# Revit family: CADS_AIRFLOWdev_AirflexPro_Round_DistributionBox_6PortNarrow_side_entry.rfa - HS
name_source: partatom
category: Duct Accessories
units: mm (PartAtom-declared; Revit-internal decimal feet)

## family parameters
Always vertical = Yes
Cut with Voids When Loaded = No
OmniClass Number = 23.75.00.00
OmniClass Title = Climate Control (HVAC)
Part Type = Breaks Into
Round Connector Dimension = Use Diameter
Shared = No
Work Plane-Based = No

## types (2) — shared parameters
6MonthlyMaintenance = Visually inspect system, clean the fan and ducting if necessary
AirflowRateRange = 54.0 L/s
AssemblyPlace = UNKNOWN
AssetType = FIXED
Body = CADS_AIRFLOWdev_SteelGalvanized
CEApproval = Yes
Color = Silver
Conn_IDia = 125 mm  [stored 0.410105 ft]
DurationUnit = Year
ExpectedServiceLife = 10
Finish = Lacquer
FireControlPanelLinks = No
Fitting Type = Ignore
Grade = Stainless
GrossWeight = 5.05 kg
Halfb1 = 150 mm  [stored 0.492126 ft]
ISO140001 = Yes
ISO90001 = Yes
IsExtendedWarranty = No
LongitudinalSeam = None
Manufacturer = Airflow Developments Ltd
ManufacturerAddress = Aidelle House
Lancaster Road
Cressex Business Park
High Wycombe
Bucks
HP123QP
ManufacturerTelephone = 01494 525252
ManufacturerWebsite = www.airflow.com
Material = Steel
NBSCode = 45-80-50/394 Ventilation ducts
NominalHeight = 200 mm  [stored 0.656168 ft]
NominalLength = 400 mm  [stored 1.31234 ft]
NominalWidth = 300 mm
PassiveHouseApproval = No
PointOfContact = Airflow Developments Ltd
ProductLiterature = https://www.airflow.com
ProductionYear = 2017
Quantity = 1
RedDotDesignAward = No
ReplacementCost = 334.62
SAPApproval = Yes
ServiceLifeDuration = 10
ServiceLifeType = EXPECTEDSERVICELIFE
Shape = Rectangular
ShippingWeight = 6.06 kg
Size = 400 x 300 x 200
Status = New
TemperatureRange = up to 40°C
Uniclass2015 = Pr_30_59_96_92:Ventilation ducts
WarrantyGuarantor = Airflow Developments Ltd
WarrantyPeriod = 0
WorkingPressure = 3000.0 Pa
b1 = 300 mm
h1 = 200 mm  [stored 0.656168 ft]
l1 = 400 mm  [stored 1.31234 ft]
zero-valued in all types: CADS_Index

## per-type parameters (varying)
| type | Constituents | Features |
| CADS_AIRFLOWdev_AirflexPro_Round_DistributionBox_6PortNarrow | 6-Spigot In-line Distribution Box . Round spigots & sound insulation fitted - Narrow | 6-Spigot In-line Distribution Box . Round spigots & sound insulation fitted - Narrow |
| CADS_AIRFLOWdev_AirflexPro_Round_DistributionBox_6PortNarrow fixed | 6-Spigot 90 degree Distribution Box . Round spigots & sound insulation fitted - Narrow | 6-Spigot 90 degree Distribution Box . Round spigots & sound insulation fitted - Narrow |

note: [stored X ft] marks values corroborated as IEEE doubles in the binary element streams (Revit-internal decimal feet)

## geometry (parser evidence)
native form markers: Blend x6, Sweep x29
no freeform markers — native parametric forms only
